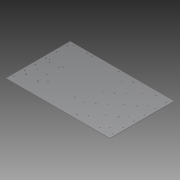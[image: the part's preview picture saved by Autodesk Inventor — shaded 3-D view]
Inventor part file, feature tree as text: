
AUTODESK INVENTOR PART (.ipt)
format: ipt  version: 2013 (Build 170138000, 138)  size: 185,856 bytes
history: native  units: in
note: dims shown in document units (in); Inventor stores cm internally (conversion verified against a paired STEP export)
features: extrude x1, sketch x1
ambient origin geometry x8: Origin, YZ Plane, XZ Plane, XY Plane, X Axis, Y Axis, Z Axis, Center Point
bodies: Solid1 (feature_tree)
feature tree (2):
  extrude  "Extrusion1"  Depth=19.4375in
  sketch  "Sketch1"  dims[d0=12.0in d4=19.4375in d6=0.15in d7=0.15in d8=1.646in d9=2.446in d11=0.1875in d12=0.1875in d13=0.1875in d14=0.1875in d15=1.5in d16=1.5in d17=8.25in d18=5.0in d19=0.2in d20=4.5in d21=0.375in d22=0.7874in d24=4.0in d25=1.1811in d27=3.5in d30=0.125in d31=0.0in d32=0.5in d33=0.2in d34=1.0in d35=0.5in d37=1.0in d38=0.3937in d40=1.0in d41=2.3622in d43=2.0in d45=3.5in d46=0.2in d47=0.7874in d49=4.25in d50=0.7874in d52=7.0in d55=0.7395in d56=0.7395in d57=2.2032in d58=0.26in d59=9.5in d63=0.2in d67=6.5in d68=1.25in d69=2.29in d70=1.75in d71=1.0in d72=2.125in d73=0.7874in d75=2.5in d76=0.7874in d78=4.5in d81=0.2in d82=4.875in d83=1.0in]
